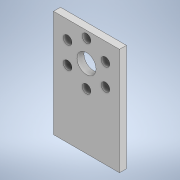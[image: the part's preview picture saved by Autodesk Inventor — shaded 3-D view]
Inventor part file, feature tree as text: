
AUTODESK INVENTOR PART (.ipt)
format: ipt  version: 2021 (Build 250183000, 183)  size: 145,408 bytes
history: native  units: in
note: dims shown in document units (in); Inventor stores cm internally (conversion verified against a paired STEP export)
features: extrude x2, sketch x2, hole x1
ambient origin geometry x8: Origin, YZ Plane, XZ Plane, XY Plane, X Axis, Y Axis, Z Axis, Center Point
bodies: Solid1 (feature_tree)
feature tree (5):
  extrude  "Extrusion1"  Depth=0.95in
  hole  "Hole1"  [1 undecoded]
  extrude  "Extrusion4"  Depth=0.0625in
  sketch  "Sketch1"  dims[d0=1.54in d1=0.95in]
  sketch  "Sketch3"  dims[d2=0.1in d3=0.0in d7=0.076in d8=0.076in d9=0.0667in d10=0.172in d11=0.375in d12=0.25in d13=0.5635in d14=0.2275in d15=0.8108in d29=2.3622in d31=0.275in d32=0.63in d33=0.125in d34=360.0deg d35=0.95in d37=0.0in d38=0.0in d16=0.75in d17=0.8108in d18=0.0625in d19=0.75in d20=0.375in d26=0.5in d27=0.0344in d28=0.5in]
note: 1 required parameter value undecoded (feature->parameter linkage not recoverable at this tier; creation-order binding heuristic only, values carry confidence <= 0.55)
